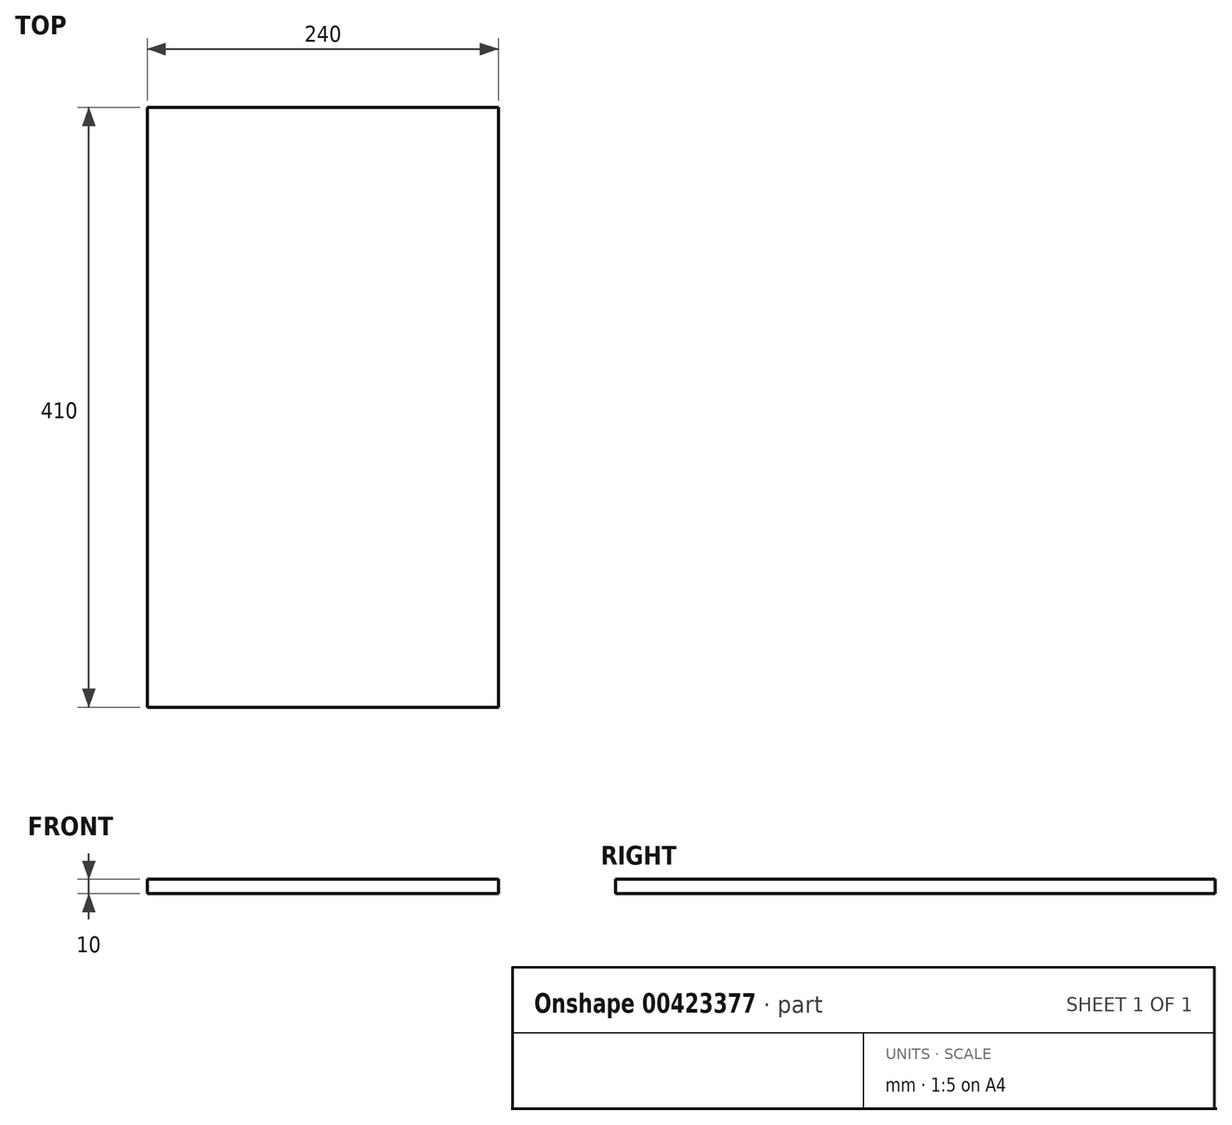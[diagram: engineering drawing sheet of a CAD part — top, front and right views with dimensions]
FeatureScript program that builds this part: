
annotation { "Feature Type Name" : "Feature", "Feature Type Description" : "" }
export const myFeature = defineFeature(function(context is Context, id is Id, definition is map)
    precondition{}
    {
        {
            var Q0;
            Q0=qCreatedBy(makeId("Top.planeOp"),FACE);
            var sketch = newSketch(context, id + "F0", { "sketchPlane" : qUnion([Q0])});
            skLineSegment(sketch, "E0.bottom", {"start": v(-56, -62.32) * mm, "end": v(184, -62.32) * mm});
            skLineSegment(sketch, "E0.top", {"start": v(-56, 347.68) * mm, "end": v(184, 347.68) * mm});
            skLineSegment(sketch, "E0.left", {"start": v(-56, -62.32) * mm, "end": v(-56, 347.68) * mm});
            skLineSegment(sketch, "E0.right", {"start": v(184, -62.32) * mm, "end": v(184, 347.68) * mm});
            skSolve(sketch);
        }
        {
            var Q0;
            Q0=makeQuery(id+"F0.imprint","IMPRINT",FACE,{"disambiguationData":[TD([[makeQuery(id+"F0.imprint","IMPRINT",EDGE,{"derivedFrom":sQuery(id+"F0.wireOp",EDGE,"E0.bottom")}),1.0]])]});
            extrude(context, id + "F1", {"entities" : qUnion([Q0]), "depth" : 10 * mm});
        }
    });
